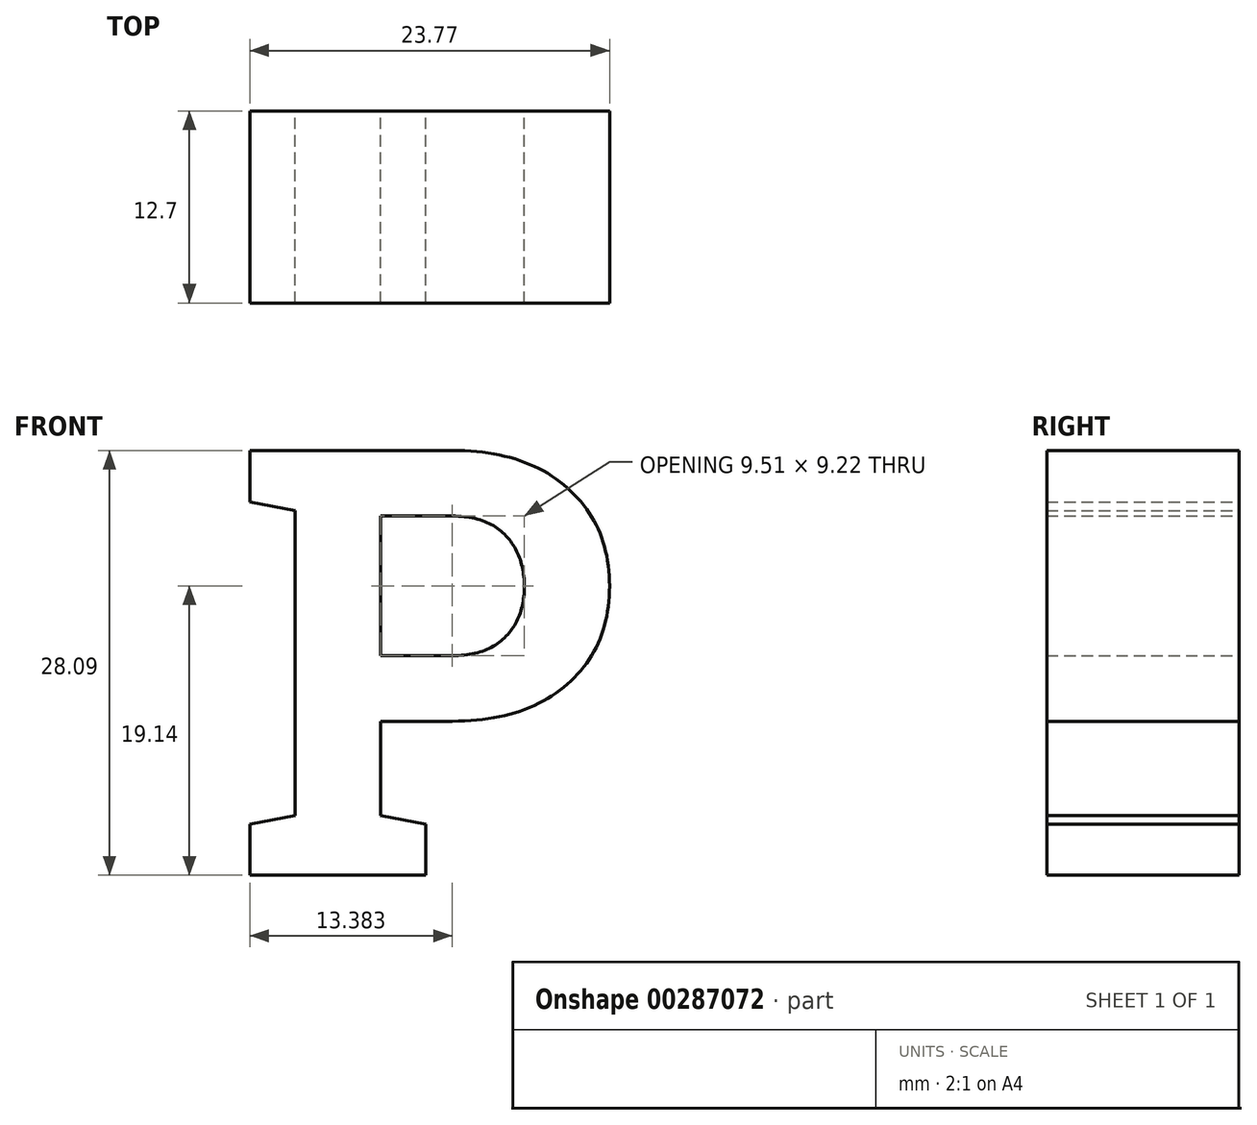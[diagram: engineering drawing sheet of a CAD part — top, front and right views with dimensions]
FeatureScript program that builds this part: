
annotation { "Feature Type Name" : "Feature", "Feature Type Description" : "" }
export const myFeature = defineFeature(function(context is Context, id is Id, definition is map)
    precondition{}
    {
        {
            var Q0;
            Q0=qCreatedBy(makeId("Front.planeOp"),FACE);
            var sketch = newSketch(context, id + "F0", { "sketchPlane" : qUnion([Q0])});
            skText(sketch, "E0", { "text": "P", "fontName": "RobotoSlab-Bold.ttf"});
            const initialGuessF0  = {"E0": [-0.0676, 0.00535, 1, 0, 0.02845]};
            skSetInitialGuess(sketch, initialGuessF0);
            skSolve(sketch);
        }
        {
            var Q0;
            Q0 = qSketchRegion(id + "F0", true);
            extrude(context, id + "F1", {"entities" : qUnion([Q0]), "depth" : 12.7 * mm});
        }
    });
